SOLIDWORKS PART (.sldprt)
format: sldprt  version: not decoded by parser v0  size: 239,104 bytes
history: native  units: mm
features: sketch x5, plane x3, cut_extrude x3, fillet x3, extrude x2, material x1, chamfer x1 (+8 scaffold rows collapsed)
feature tree (26):
  scaffold x8  (default folders/planes/origin — collapsed)
  material  "Duranickel(R) 301"
  plane  "Alzado"
  plane  "Planta"
  plane  "Vista lateral"
  sketch  "Croquis1"  dims[D1=14.0mm D2=12.6mm]
  extrude  "Extruir1"  Depth=8.3mm
  sketch  "Croquis2"  dims[D1=9.5mm D2=1.7mm]
  cut_extrude  "Cortar-Extruir1"  Depth=7.3mm
  fillet  "Redondeo1"  Radius=0.5mm
  sketch  "Croquis3"  dims[D1=1.4mm D2=1.0mm D3=1.0mm D4=1.4mm D5=0.5mm]
  cut_extrude  "Cortar-Extruir2"  Depth=7.3mm
  fillet  "Redondeo2"  Radius=0.5mm
  sketch  "Croquis4"  dims[D1=7.7mm D2=2.35mm D3=2.3mm D4=4.7mm D5=1.8mm D6=0.9mm]
  extrude  "Extruir2"  [1 undecoded]
  sketch  "Croquis5"  dims[D5=0.6mm D6=0.6mm D7=0.6mm D1=0.8mm D2=2.2mm D3=1.5mm D4=0.75mm]
  cut_extrude  "Cortar-Extruir3"  Depth=7.3mm
  chamfer  "Chaflán1"  Distance=0.4mm Angle=45deg
  fillet  "Redondeo3"  Radius=0.2mm
decode coverage: 13 of 14 modeling features carry decoded parameters
note: 1 parameter value undecoded
note: suppression state not decoded; provenance and decode notes live in map.json
